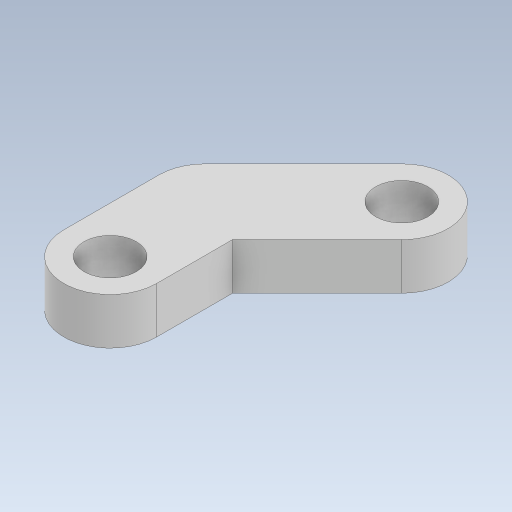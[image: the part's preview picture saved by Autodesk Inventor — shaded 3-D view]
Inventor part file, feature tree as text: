
AUTODESK INVENTOR PART (.ipt)
format: ipt  version: 2023 (Build 270158000, 158)  size: 113,152 bytes
history: native  units: in
note: dims shown in document units (in); Inventor stores cm internally (conversion verified against a paired STEP export)
features: sketch x2, extrude x1, hole x1
ambient origin geometry x8: Origin, YZ Plane, XZ Plane, XY Plane, X Axis, Y Axis, Z Axis, Center Point
bodies: Solid1 (feature_tree)
feature tree (4):
  extrude  "Extrusion1"  Depth=0.4724in
  hole  "Hole1"  [1 undecoded]
  sketch  "Sketch1"  dims[d0=0.4724in d1=0.5in]
  sketch  "Sketch2"  dims[d2=0.9843in d3=135.0deg d4=0.2362in d5=0.0in d6=0.2362in d7=0.266in d8=0.2362in d9=0.507in d10=0.0787in d11=0.5635in d12=0.5in d13=0.8108in]
note: 1 required parameter value undecoded (feature->parameter linkage not recoverable at this tier; creation-order binding heuristic only, values carry confidence <= 0.55)
